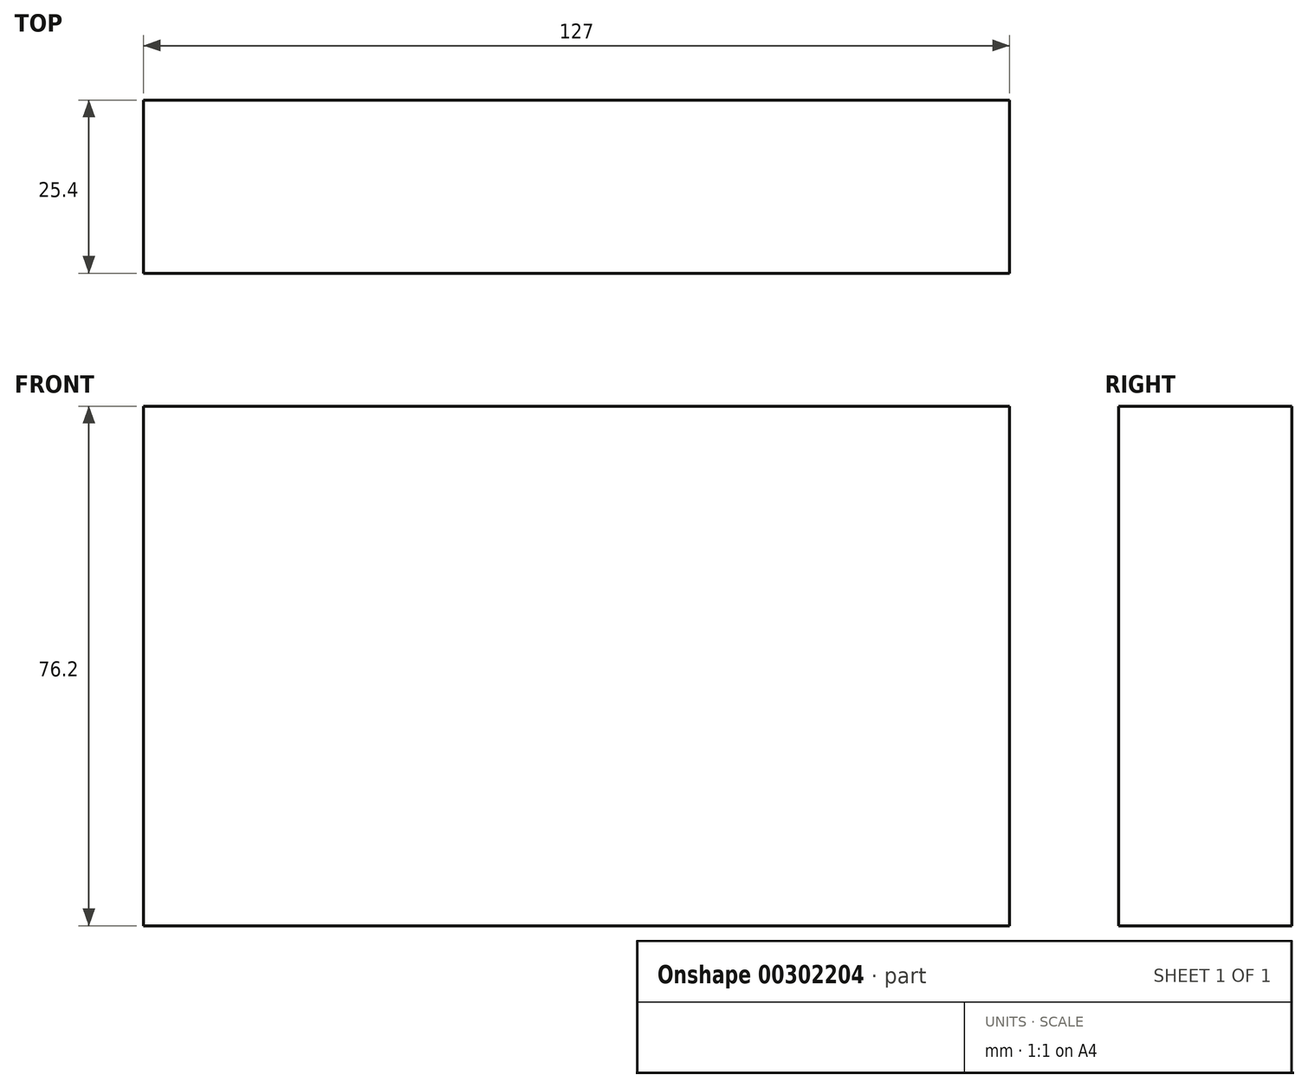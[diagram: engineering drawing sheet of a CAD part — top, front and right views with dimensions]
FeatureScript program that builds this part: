
annotation { "Feature Type Name" : "Feature", "Feature Type Description" : "" }
export const myFeature = defineFeature(function(context is Context, id is Id, definition is map)
    precondition{}
    {
        {
            var Q0;
            Q0=qCreatedBy(makeId("Front.planeOp"),FACE);
            var sketch = newSketch(context, id + "F0", { "sketchPlane" : qUnion([Q0])});
            skLineSegment(sketch, "E0.bottom", {"start": v(63.5, 38.1) * mm, "end": v(-63.5, 38.1) * mm});
            skLineSegment(sketch, "E0.top", {"start": v(63.5, -38.1) * mm, "end": v(-63.5, -38.1) * mm});
            skLineSegment(sketch, "E0.left", {"start": v(63.5, 38.1) * mm, "end": v(63.5, -38.1) * mm});
            skLineSegment(sketch, "E0.right", {"start": v(-63.5, 38.1) * mm, "end": v(-63.5, -38.1) * mm});
            skPoint(sketch, "E0.middle", {"position": v(0, 0) * mm});
            skSolve(sketch);
        }
        {
            var Q0;
            Q0=makeQuery(id+"F0.imprint","IMPRINT",FACE,{"disambiguationData":[TD([[makeQuery(id+"F0.imprint","IMPRINT",EDGE,{"derivedFrom":sQuery(id+"F0.wireOp",EDGE,"E0.bottom")}),1.0]])]});
            extrude(context, id + "F1", {"entities" : qUnion([Q0]), "depth" : 25.4 * mm});
        }
    });
